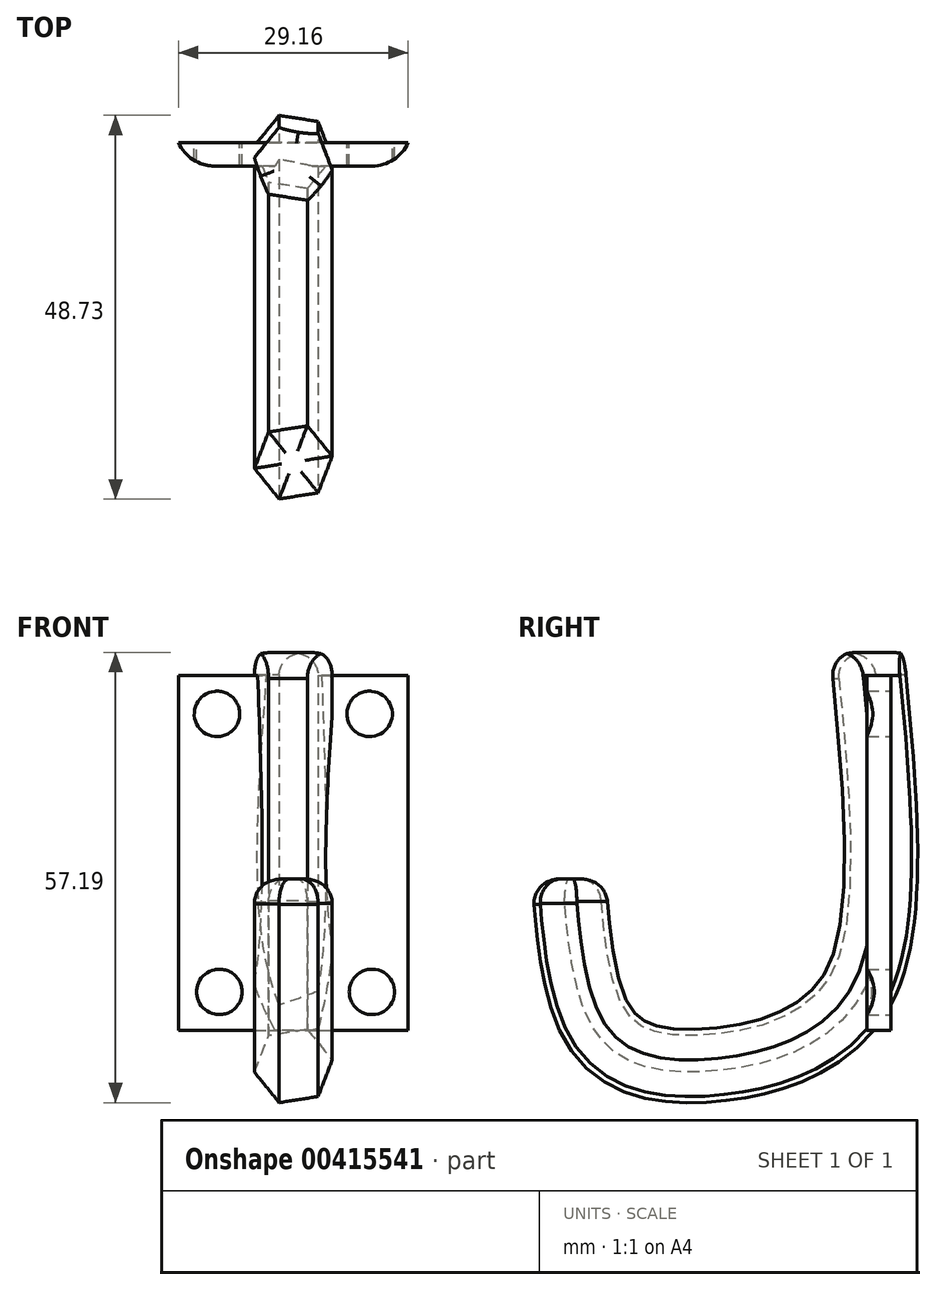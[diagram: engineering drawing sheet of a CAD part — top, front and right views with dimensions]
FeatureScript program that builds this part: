
annotation { "Feature Type Name" : "Feature", "Feature Type Description" : "" }
export const myFeature = defineFeature(function(context is Context, id is Id, definition is map)
    precondition{}
    {
        {
            var Q0;
            Q0=qCreatedBy(makeId("Right.planeOp"),FACE);
            var sketch = newSketch(context, id + "F0", { "sketchPlane" : qUnion([Q0])});
            skFitSpline(sketch, "E0", {"points": [v(0, 0) * mm, v(0, -40.12) * mm, v(-8.28, -49.43) * mm, v(-18.2, -52.26) * mm, v(-28.77, -51.63) * mm, v(-35.08, -45.48) * mm, v(-37.6, -32.24) * mm, v(-37.92, -28.77) * mm], "startDerivative": vector(18.18, -184.69) * mm, "endDerivative": vector(-3.35, 36.55) * mm});
            skSolve(sketch);
        }
        {
            var Q0;
            Q0=qCreatedBy(makeId("Top.planeOp"),FACE);
            var sketch = newSketch(context, id + "F1", { "sketchPlane" : qUnion([Q0])});
            skCircle(sketch, "E1.cCircle", {"center": v(0, 0) * mm, "radius": 4.33 * mm, "construction": true});
            skLineSegment(sketch, "E1.0", {"start": v(3.14, 3.89) * mm, "end": v(4.94, -0.78) * mm});
            skLineSegment(sketch, "E1.1", {"start": v(4.94, -0.78) * mm, "end": v(1.8, -4.67) * mm});
            skLineSegment(sketch, "E1.2", {"start": v(1.8, -4.67) * mm, "end": v(-3.14, -3.89) * mm});
            skLineSegment(sketch, "E1.3", {"start": v(-3.14, -3.89) * mm, "end": v(-4.94, 0.78) * mm});
            skLineSegment(sketch, "E1.4", {"start": v(-4.94, 0.78) * mm, "end": v(-1.8, 4.67) * mm});
            skLineSegment(sketch, "E1.5", {"start": v(-1.8, 4.67) * mm, "end": v(3.14, 3.89) * mm});
            skPoint(sketch, "E1.0.midPoint", {"position": v(4.04, 1.55) * mm});
            skSolve(sketch);
        }
        {
            var Q0;
            Q0=makeQuery(id+"F1.imprint","IMPRINT",FACE,{"disambiguationData":[TD([[makeQuery(id+"F1.imprint","IMPRINT",EDGE,{"derivedFrom":sQuery(id+"F1.wireOp",EDGE,"E1.0")}),-1.0]])]});
            var Q1;
            Q1=sQuery(id+"F0.wireOp",EDGE,"E0");
            sweep(context, id + "F2", {"profiles" : qUnion([Q0]), "path" : qUnion([Q1])});
        }
        {
            var Q0;
            Q0=makeQuery(id+"F2.opSweep","CAP_FACE",FACE,{"disambiguationData":[OSD([sQuery(id+"F0.wireOp",VERTEX,"E0.end"),sQuery(id+"F1.wireOp",EDGE,"E1.0"),sQuery(id+"F1.wireOp",EDGE,"E1.1"),sQuery(id+"F1.wireOp",EDGE,"E1.2"),sQuery(id+"F1.wireOp",EDGE,"E1.3"),sQuery(id+"F1.wireOp",EDGE,"E1.4"),sQuery(id+"F1.wireOp",EDGE,"E1.5")])],"isStart":false});
            var Q1;
            Q1=makeQuery(id+"F2.opSweep","CAP_EDGE",EDGE,{"disambiguationData":[OSD([sQuery(id+"F0.wireOp",VERTEX,"E0.start"),sQuery(id+"F1.wireOp",EDGE,"E1.2")])],"isStart":true});
            var Q2;
            Q2=makeQuery(id+"F2.opSweep","CAP_EDGE",EDGE,{"disambiguationData":[OSD([sQuery(id+"F0.wireOp",VERTEX,"E0.start"),sQuery(id+"F1.wireOp",EDGE,"E1.0")])],"isStart":true});
            var Q3;
            Q3=makeQuery(id+"F2.opSweep","CAP_EDGE",EDGE,{"disambiguationData":[OSD([sQuery(id+"F0.wireOp",VERTEX,"E0.start"),sQuery(id+"F1.wireOp",EDGE,"E1.4")])],"isStart":true});
            fillet(context, id + "F3", {"entities" : qUnion([Q0, Q1, Q2, Q3]), "radius" : 3 * mm, "tangentPropagation" : true, "allowEdgeOverflow" : false});
        }
        {
            var Q0;
            Q0=qCreatedBy(makeId("Front.planeOp"),FACE);
            var sketch = newSketch(context, id + "F4", { "sketchPlane" : qUnion([Q0])});
            skLineSegment(sketch, "E2.bottom", {"start": v(-14.58, -2.92) * mm, "end": v(14.58, -2.92) * mm});
            skLineSegment(sketch, "E2.top", {"start": v(-14.58, -48) * mm, "end": v(14.58, -48) * mm});
            skLineSegment(sketch, "E2.left", {"start": v(-14.58, -2.92) * mm, "end": v(-14.58, -48) * mm});
            skLineSegment(sketch, "E2.right", {"start": v(14.58, -2.92) * mm, "end": v(14.58, -48) * mm});
            skPoint(sketch, "E2.middle", {"position": v(0, -25.46) * mm});
            skSolve(sketch);
        }
        {
            var Q0;
            Q0=makeQuery(id+"F4.imprint","IMPRINT",FACE,{"disambiguationData":[TD([[makeQuery(id+"F4.imprint","IMPRINT",EDGE,{"derivedFrom":sQuery(id+"F4.wireOp",EDGE,"E2.bottom")}),-1.0]])]});
            extrude(context, id + "F5", {"entities" : qUnion([Q0]), "operationType" : NewBodyOperationType.ADD, "oppositeDirection" : true, "depth" : 3 * mm});
        }
        {
            var Q0;
            Q0=makeQuery(id+"F5.opExtrude","CAP_FACE",FACE,{"disambiguationData":[OSD([sQuery(id+"F4.wireOp",EDGE,"E2.bottom"),sQuery(id+"F4.wireOp",EDGE,"E2.top"),sQuery(id+"F4.wireOp",EDGE,"E2.left"),sQuery(id+"F4.wireOp",EDGE,"E2.right")])],"isStart":false});
            var sketch = newSketch(context, id + "F6", { "sketchPlane" : qUnion([Q0])});
            skCircle(sketch, "E3", {"center": v(-9.7, -7.8) * mm, "radius": 2.89 * mm});
            skCircle(sketch, "E4.0.1.0", {"center": v(-10, -43.12) * mm, "radius": 2.89 * mm});
            skCircle(sketch, "E4.1.0.0", {"center": v(9.7, -7.8) * mm, "radius": 2.89 * mm});
            skCircle(sketch, "E4.1.1.0", {"center": v(9.4, -43.12) * mm, "radius": 2.89 * mm});
            skCircle(sketch, "E4.2.0.0", {"center": v(29.08, -7.8) * mm, "radius": 2.89 * mm});
            skCircle(sketch, "E4.2.1.0", {"center": v(28.78, -43.12) * mm, "radius": 2.89 * mm});
            skLineSegment(sketch, "E4.direction1", {"start": v(-9.7, -7.8) * mm, "end": v(9.7, -7.8) * mm, "construction": true});
            skLineSegment(sketch, "E4.direction2", {"start": v(-9.7, -7.8) * mm, "end": v(-10, -43.12) * mm, "construction": true});
            skSolve(sketch);
        }
        {
            var Q0;
            Q0=makeQuery(id+"F6.imprint","IMPRINT",FACE,{"disambiguationData":[TD([[makeQuery(id+"F6.imprint","IMPRINT",EDGE,{"derivedFrom":sQuery(id+"F6.wireOp",EDGE,"E4.2.0.0")}),1.0]])]});
            var Q1;
            Q1=makeQuery(id+"F6.imprint","IMPRINT",FACE,{"disambiguationData":[TD([[makeQuery(id+"F6.imprint","IMPRINT",EDGE,{"derivedFrom":sQuery(id+"F6.wireOp",EDGE,"E4.2.1.0")}),1.0]])]});
            var Q2;
            Q2=makeQuery(id+"F6.imprint","IMPRINT",FACE,{"disambiguationData":[TD([[makeQuery(id+"F6.imprint","IMPRINT",EDGE,{"derivedFrom":sQuery(id+"F6.wireOp",EDGE,"E4.0.1.0")}),1.0]])]});
            var Q3;
            Q3=makeQuery(id+"F6.imprint","IMPRINT",FACE,{"disambiguationData":[TD([[makeQuery(id+"F6.imprint","IMPRINT",EDGE,{"derivedFrom":sQuery(id+"F6.wireOp",EDGE,"E4.1.1.0")}),1.0]])]});
            var Q4;
            Q4=makeQuery(id+"F6.imprint","IMPRINT",FACE,{"disambiguationData":[TD([[makeQuery(id+"F6.imprint","IMPRINT",EDGE,{"derivedFrom":sQuery(id+"F6.wireOp",EDGE,"E3")}),1.0]])]});
            var Q5;
            Q5=makeQuery(id+"F6.imprint","IMPRINT",FACE,{"disambiguationData":[TD([[makeQuery(id+"F6.imprint","IMPRINT",EDGE,{"derivedFrom":sQuery(id+"F6.wireOp",EDGE,"E4.1.0.0")}),1.0]])]});
            extrude(context, id + "F7", {"entities" : qUnion([Q0, Q1, Q2, Q3, Q4, Q5]), "operationType" : NewBodyOperationType.REMOVE, "oppositeDirection" : true, "depth" : 25 * mm});
        }
        {
            var Q0;
            Q0=makeQuery(id+"F5.opExtrude","CAP_EDGE",EDGE,{"disambiguationData":[OSD([sQuery(id+"F4.wireOp",EDGE,"E2.left")])],"isStart":true});
            var Q1;
            Q1=makeQuery(id+"F5.opExtrude","CAP_EDGE",EDGE,{"disambiguationData":[OSD([sQuery(id+"F4.wireOp",EDGE,"E2.right")])],"isStart":true});
            fillet(context, id + "F8", {"entities" : qUnion([Q0, Q1]), "radius" : 5 * mm, "tangentPropagation" : true, "allowEdgeOverflow" : false});
        }
    });
